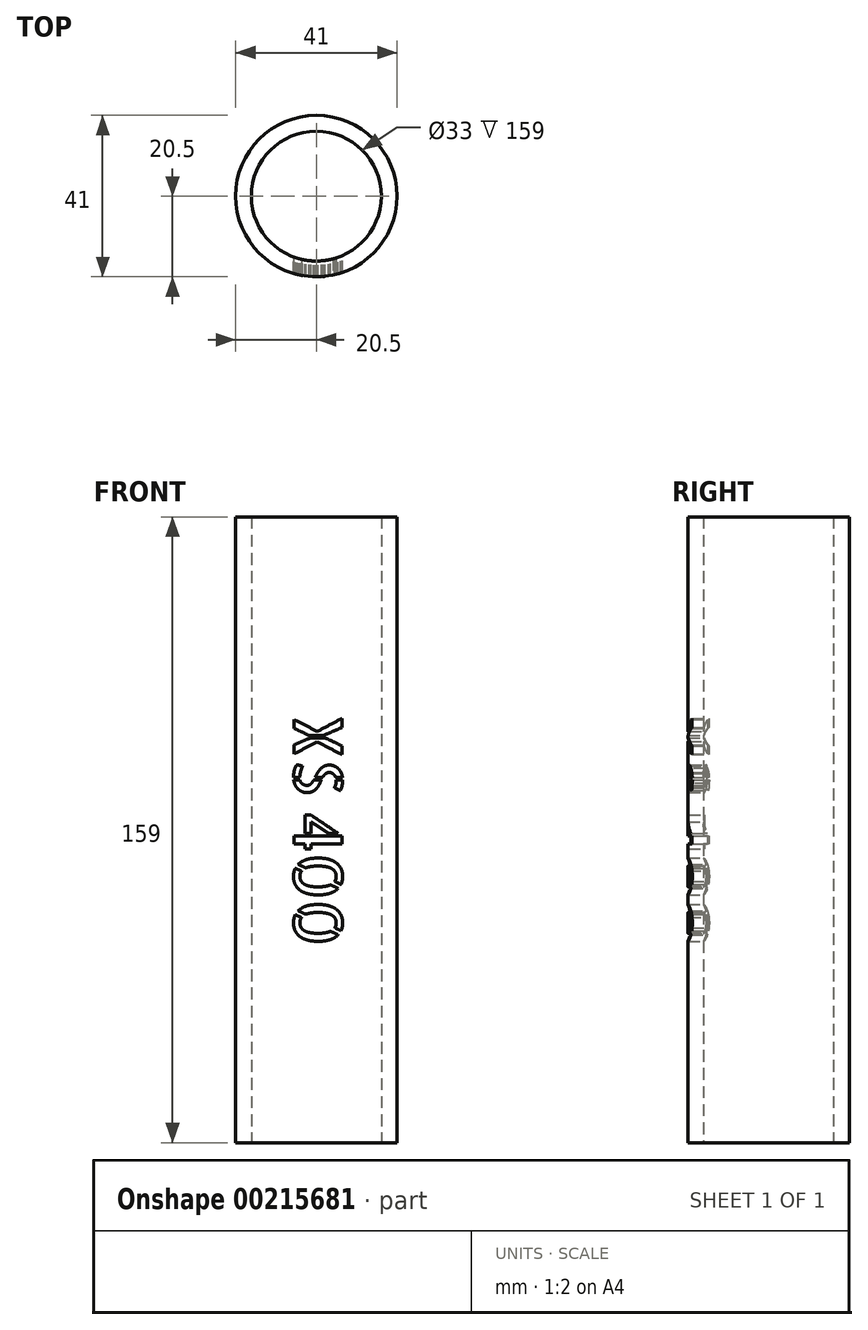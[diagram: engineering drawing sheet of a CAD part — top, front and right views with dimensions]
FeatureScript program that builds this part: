
annotation { "Feature Type Name" : "Feature", "Feature Type Description" : "" }
export const myFeature = defineFeature(function(context is Context, id is Id, definition is map)
    precondition{}
    {
        {
            var Q0;
            Q0=qCreatedBy(makeId("Top.planeOp"),FACE);
            var sketch = newSketch(context, id + "F0", { "sketchPlane" : qUnion([Q0])});
            skCircle(sketch, "E0", {"center": v(0, 0) * mm, "radius": 16.5 * mm});
            skCircle(sketch, "E1", {"center": v(0, 0) * mm, "radius": 20.5 * mm});
            skSolve(sketch);
        }
        {
            var Q0;
            Q0=makeQuery(id+"F0.imprint","IMPRINT",FACE,{"disambiguationData":[TD([[makeQuery(id+"F0.imprint","IMPRINT",EDGE,{"derivedFrom":sQuery(id+"F0.wireOp",EDGE,"E0")}),-1.0]])]});
            extrude(context, id + "F1", {"entities" : qUnion([Q0]), "depth" : 159 * mm});
        }
        {
            var Q0;
            Q0=qCreatedBy(makeId("Front.planeOp"),FACE);
            var sketch = newSketch(context, id + "F2", { "sketchPlane" : qUnion([Q0])});
            skText(sketch, "E2", { "text": "XS 400\n", "fontName": "AllertaStencil-Regular.ttf"});
            skLineSegment(sketch, "E3", {"start": v(0, 159.42) * mm, "end": v(0, 0) * mm, "construction": true});
            const initialGuessF2  = {"E2": [-0.00572, 0.109, 0, -1, 0.01222]};
            skSetInitialGuess(sketch, initialGuessF2);
            skSolve(sketch);
        }
        {
            var Q0;
            Q0 = qSketchRegion(id + "F2", true);
            extrude(context, id + "F3", {"entities" : qUnion([Q0]), "operationType" : NewBodyOperationType.REMOVE, "depth" : 30 * mm});
        }
    });
